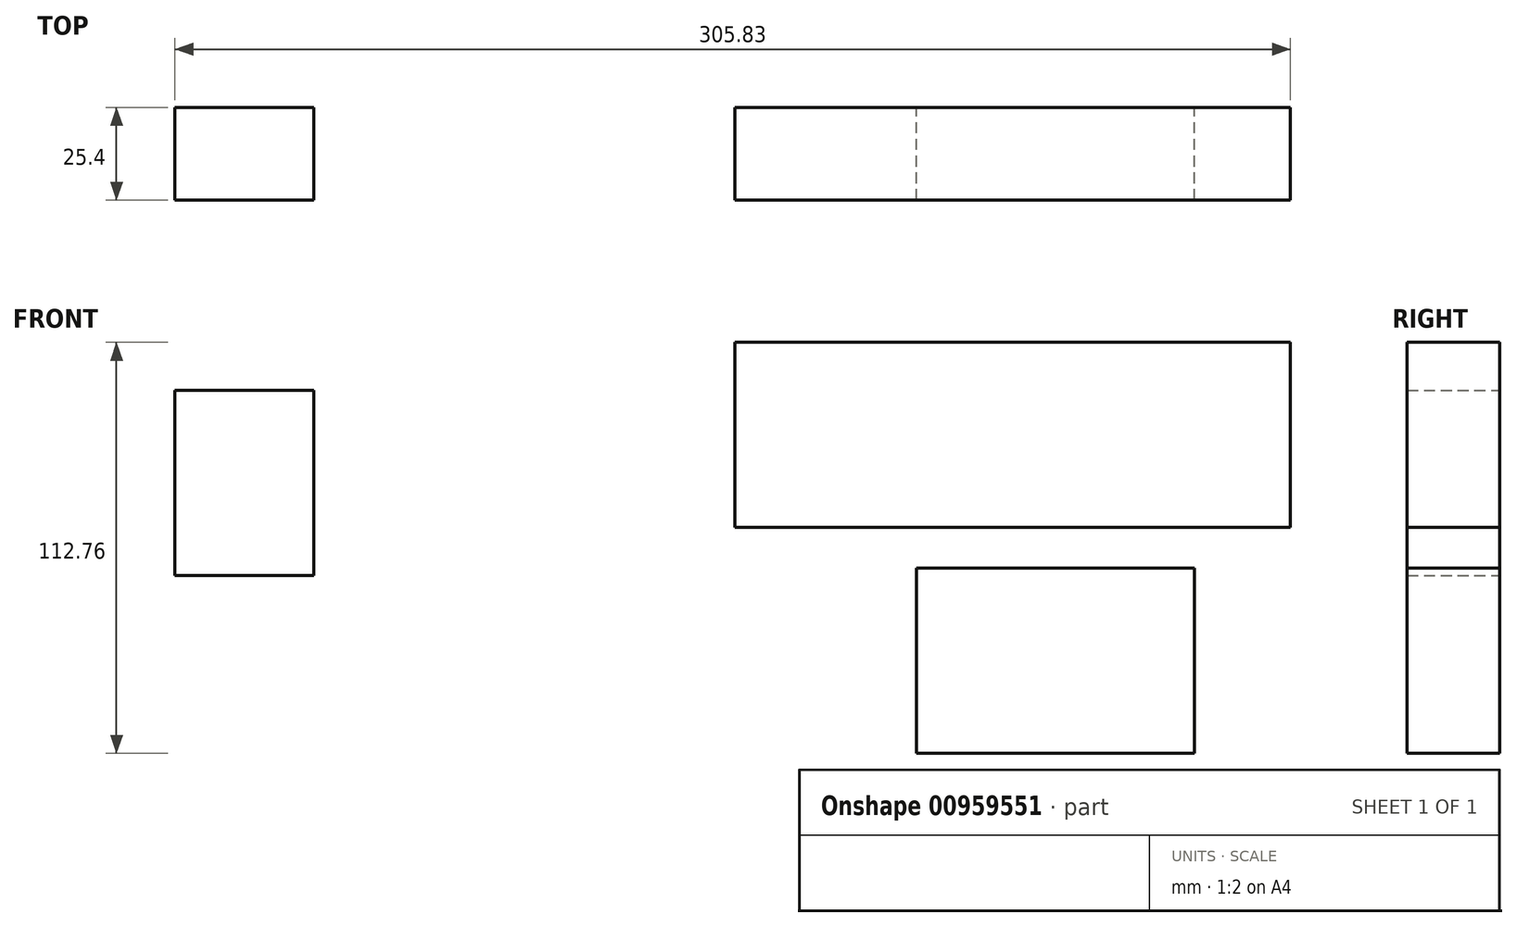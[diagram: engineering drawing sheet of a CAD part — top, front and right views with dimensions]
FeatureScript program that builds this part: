
annotation { "Feature Type Name" : "Feature", "Feature Type Description" : "" }
export const myFeature = defineFeature(function(context is Context, id is Id, definition is map)
    precondition{}
    {
        {
            var Q0;
            Q0=qCreatedBy(makeId("Front.planeOp"),FACE);
            var sketch = newSketch(context, id + "F0", { "sketchPlane" : qUnion([Q0])});
            skLineSegment(sketch, "E0.bottom", {"start": v(-110.33, 48.93) * mm, "end": v(42.07, 48.93) * mm});
            skLineSegment(sketch, "E0.top", {"start": v(-110.33, -1.87) * mm, "end": v(42.07, -1.87) * mm});
            skLineSegment(sketch, "E0.left", {"start": v(-110.33, 48.93) * mm, "end": v(-110.33, -1.87) * mm});
            skLineSegment(sketch, "E0.right", {"start": v(42.07, 48.93) * mm, "end": v(42.07, -1.87) * mm});
            skSolve(sketch);
        }
        {
            var Q0;
            Q0=makeQuery(id+"F0.imprint","IMPRINT",FACE,{"disambiguationData":[TD([[makeQuery(id+"F0.imprint","IMPRINT",EDGE,{"derivedFrom":sQuery(id+"F0.wireOp",EDGE,"E0.bottom")}),-1.0]])]});
            extrude(context, id + "F1", {"entities" : qUnion([Q0]), "depth" : 25.4 * mm, "offsetDistance" : 25.4 * mm});
        }
        {
            var Q0;
            Q0=qCreatedBy(makeId("Front.planeOp"),FACE);
            var sketch = newSketch(context, id + "F2", { "sketchPlane" : qUnion([Q0])});
            skLineSegment(sketch, "E1.bottom", {"start": v(-60.44, -13.03) * mm, "end": v(15.76, -13.03) * mm});
            skLineSegment(sketch, "E1.top", {"start": v(-60.44, -63.83) * mm, "end": v(15.76, -63.83) * mm});
            skLineSegment(sketch, "E1.left", {"start": v(-60.44, -13.03) * mm, "end": v(-60.44, -63.83) * mm});
            skLineSegment(sketch, "E1.right", {"start": v(15.76, -13.03) * mm, "end": v(15.76, -63.83) * mm});
            skSolve(sketch);
        }
        {
            var Q0;
            Q0=makeQuery(id+"F2.imprint","IMPRINT",FACE,{"disambiguationData":[TD([[makeQuery(id+"F2.imprint","IMPRINT",EDGE,{"derivedFrom":sQuery(id+"F2.wireOp",EDGE,"E1.bottom")}),-1.0]])]});
            extrude(context, id + "F3", {"entities" : qUnion([Q0]), "depth" : 25.4 * mm, "offsetDistance" : 25.4 * mm});
        }
        {
            var Q0;
            Q0=qCreatedBy(makeId("Front.planeOp"),FACE);
            var sketch = newSketch(context, id + "F4", { "sketchPlane" : qUnion([Q0])});
            skLineSegment(sketch, "E2.bottom", {"start": v(-225.66, 35.72) * mm, "end": v(-263.76, 35.72) * mm});
            skLineSegment(sketch, "E2.top", {"start": v(-225.66, -15.08) * mm, "end": v(-263.76, -15.08) * mm});
            skLineSegment(sketch, "E2.left", {"start": v(-225.66, 35.72) * mm, "end": v(-225.66, -15.08) * mm});
            skLineSegment(sketch, "E2.right", {"start": v(-263.76, 35.72) * mm, "end": v(-263.76, -15.08) * mm});
            skPoint(sketch, "E2.middle", {"position": v(-244.7, 10.32) * mm});
            skSolve(sketch);
        }
        {
            var Q0;
            Q0=makeQuery(id+"F4.imprint","IMPRINT",FACE,{"disambiguationData":[TD([[makeQuery(id+"F4.imprint","IMPRINT",EDGE,{"derivedFrom":sQuery(id+"F4.wireOp",EDGE,"E2.bottom")}),1.0]])]});
            extrude(context, id + "F5", {"entities" : qUnion([Q0]), "depth" : 25.4 * mm, "offsetDistance" : 25.4 * mm});
        }
    });
